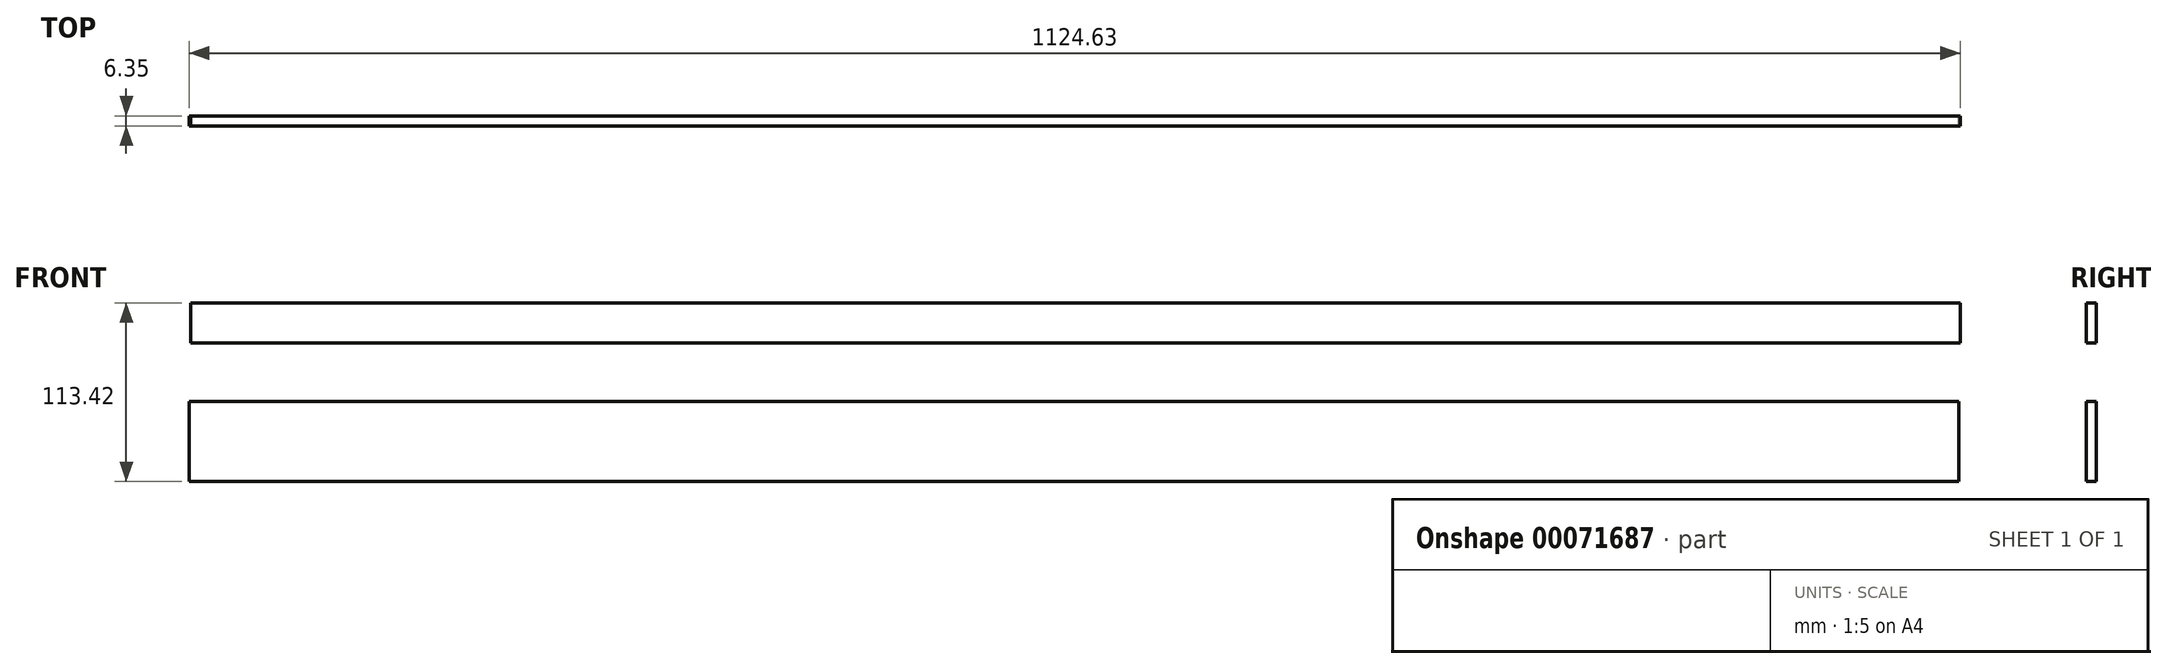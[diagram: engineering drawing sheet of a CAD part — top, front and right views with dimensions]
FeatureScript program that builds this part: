
annotation { "Feature Type Name" : "Feature", "Feature Type Description" : "" }
export const myFeature = defineFeature(function(context is Context, id is Id, definition is map)
    precondition{}
    {
        {
            var Q0;
            Q0=qCreatedBy(makeId("Front.planeOp"),FACE);
            var sketch = newSketch(context, id + "F0", { "sketchPlane" : qUnion([Q0])});
            skLineSegment(sketch, "E0.bottom", {"start": v(955.84, 100.4) * mm, "end": v(-168.1, 100.4) * mm});
            skLineSegment(sketch, "E0.top", {"start": v(955.84, 75) * mm, "end": v(-168.1, 75) * mm});
            skLineSegment(sketch, "E0.left", {"start": v(955.84, 100.4) * mm, "end": v(955.84, 75) * mm});
            skLineSegment(sketch, "E0.right", {"start": v(-168.1, 100.4) * mm, "end": v(-168.1, 75) * mm});
            skLineSegment(sketch, "E1.bottom", {"start": v(955.16, 37.78) * mm, "end": v(-168.8, 37.78) * mm});
            skLineSegment(sketch, "E1.top", {"start": v(955.16, -13.02) * mm, "end": v(-168.8, -13.02) * mm});
            skLineSegment(sketch, "E1.left", {"start": v(955.16, 37.78) * mm, "end": v(955.16, -13.02) * mm});
            skLineSegment(sketch, "E1.right", {"start": v(-168.8, 37.78) * mm, "end": v(-168.8, -13.02) * mm});
            skSolve(sketch);
        }
        {
            var Q0;
            Q0=makeQuery(id+"F0.imprint","IMPRINT",FACE,{"disambiguationData":[TD([[makeQuery(id+"F0.imprint","IMPRINT",EDGE,{"derivedFrom":sQuery(id+"F0.wireOp",EDGE,"E0.bottom")}),1.0]])]});
            var Q1;
            Q1=makeQuery(id+"F0.imprint","IMPRINT",FACE,{"disambiguationData":[TD([[makeQuery(id+"F0.imprint","IMPRINT",EDGE,{"derivedFrom":sQuery(id+"F0.wireOp",EDGE,"E1.bottom")}),1.0]])]});
            extrude(context, id + "F1", {"entities" : qUnion([Q0, Q1]), "depth" : 6.35 * mm});
        }
    });
